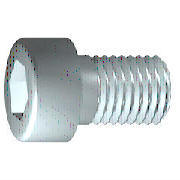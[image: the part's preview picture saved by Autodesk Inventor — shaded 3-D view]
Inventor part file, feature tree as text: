
AUTODESK INVENTOR PART (.ipt)
format: ipt  version: 2018 (Build 220112000, 112)  size: 196,096 bytes
history: native  units: mm (DEFAULTED — no unit token found)
features: sketch x2, extrude x1, plane x1, fillet x1
ambient origin geometry x7: Origin, YZ Plane, XY Plane, X Axis, Y Axis, Z Axis, Center Point
bodies: Solid1 (feature_tree), Body (feature_tree)
feature tree (5):
  extrude  "Slot"  Depth=2.0mm
  plane  "Work Plane1"
  fillet  "Fillet2"  Radius=2.0mm
  sketch  "Sketch1"  dims[d1=5.0mm d2=0.24548mm d3=2.0mm]
  sketch  "Sketch2"  dims[d4=1.0mm d5=60.0deg d6=2.0mm d7=2.0mm d8=1.732051mm d9=3.8mm d10=90.0deg d11=10.0mm d12=0.0mm d13=5.0mm d14=0.0mm d15=0.24538mm d16=0.24538mm d17=0.2mm d19=0.0mm d26=6.0mm d27=45.0deg d28=0.0mm d29=0.0mm d30=0.1mm]
